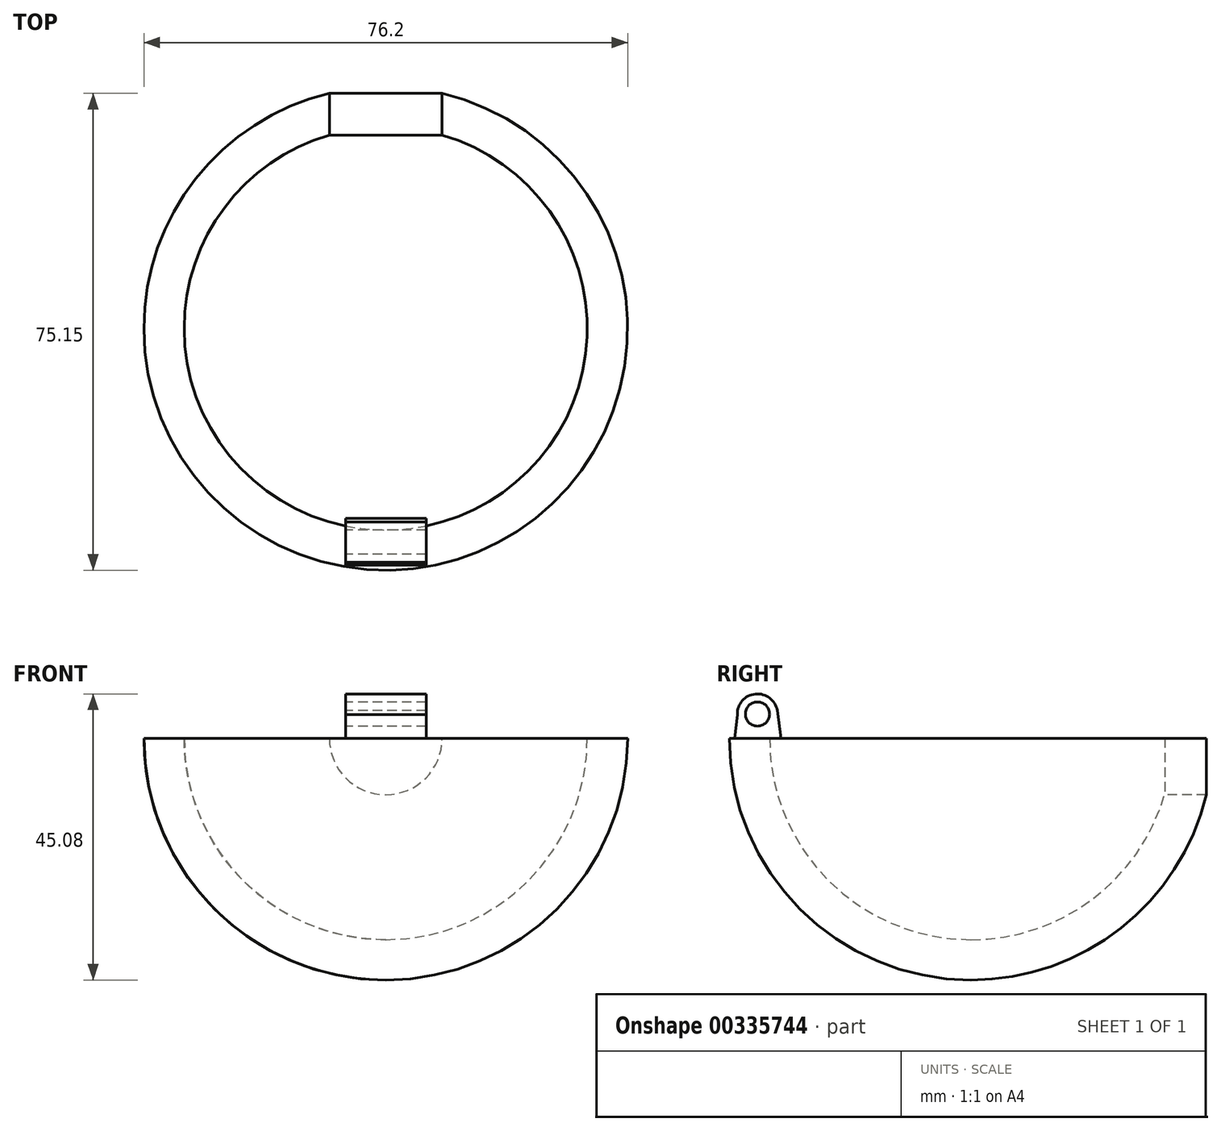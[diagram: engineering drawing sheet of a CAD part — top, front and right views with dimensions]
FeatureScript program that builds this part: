
annotation { "Feature Type Name" : "Feature", "Feature Type Description" : "" }
export const myFeature = defineFeature(function(context is Context, id is Id, definition is map)
    precondition{}
    {
        {
            var Q0;
            Q0=qCreatedBy(makeId("Front.planeOp"),FACE);
            var sketch = newSketch(context, id + "F0", { "sketchPlane" : qUnion([Q0])});
            skArc(sketch, "E0", {"start": v(-38.1, 0) * mm, "mid": v(-26.94, -26.94) * mm, "end": v(0, -38.1) * mm});
            skLineSegment(sketch, "E1", {"start": v(-38.1, 0) * mm, "end": v(-31.75, 0) * mm});
            skLineSegment(sketch, "E2", {"start": v(0, -31.75) * mm, "end": v(0, -38.1) * mm});
            skArc(sketch, "E3.0", {"start": v(-31.75, 0) * mm, "mid": v(-22.45, -22.45) * mm, "end": v(0, -31.75) * mm});
            skSolve(sketch);
        }
        {
            var Q0;
            Q0=makeQuery(id+"F0.imprint","IMPRINT",FACE,{"disambiguationData":[TD([[makeQuery(id+"F0.imprint","IMPRINT",EDGE,{"derivedFrom":sQuery(id+"F0.wireOp",EDGE,"E0")}),1.0]])]});
            var Q1;
            Q1=sQuery(id+"F0.wireOp",EDGE,"E2");
            revolve(context, id + "F1", {"entities" : qUnion([Q0]), "axis" : qUnion([Q1]), "revolveType" : RevolveType.FULL});
        }
        {
            var Q0;
            Q0=qCreatedBy(makeId("Front.planeOp"),FACE);
            var sketch = newSketch(context, id + "F2", { "sketchPlane" : qUnion([Q0])});
            skCircle(sketch, "E4", {"center": v(0, 0) * mm, "radius": 8.9 * mm});
            skSolve(sketch);
        }
        {
            var Q0;
            Q0=makeQuery(id+"F2.imprint","IMPRINT",FACE,{"disambiguationData":[TD([[makeQuery(id+"F2.imprint","IMPRINT",EDGE,{"derivedFrom":sQuery(id+"F2.wireOp",EDGE,"E4")}),1.0]])]});
            extrude(context, id + "F3", {"entities" : qUnion([Q0]), "operationType" : NewBodyOperationType.REMOVE, "endBound" : BoundingType.THROUGH_ALL, "oppositeDirection" : true, "depth" : 25.4 * mm});
        }
        {
            var Q0;
            Q0=qCreatedBy(makeId("Right.planeOp"),FACE);
            var sketch = newSketch(context, id + "F4", { "sketchPlane" : qUnion([Q0])});
            skLineSegment(sketch, "E5.0.0", {"start": v(-31.75, 0) * mm, "end": v(-38.1, 0) * mm});
            skPoint(sketch, "E5.0.3.end.orphan", {"position": v(37.05, 0) * mm});
            skPoint(sketch, "E5.0.3.start.orphan", {"position": v(30.48, 0) * mm});
            skPoint(sketch, "E5.0.1.end.orphan", {"position": v(30.48, 0) * mm});
            skPoint(sketch, "E5.0.1.start.orphan", {"position": v(37.05, 0) * mm});
            skCircle(sketch, "E6", {"center": v(-33.65, 3.8) * mm, "radius": 1.9 * mm});
            skArc(sketch, "E7.0", {"start": v(-30.5, 4.1) * mm, "mid": v(-33.83, 6.98) * mm, "end": v(-36.83, 3.74) * mm});
            skLineSegment(sketch, "E8", {"start": v(-36.83, 3.74) * mm, "end": v(-37.27, 0) * mm});
            skLineSegment(sketch, "E9", {"start": v(-37.27, 0) * mm, "end": v(-29.94, 0) * mm});
            skLineSegment(sketch, "E10", {"start": v(-29.94, 0) * mm, "end": v(-30.53, 4.37) * mm});
            skSolve(sketch);
        }
        {
            var Q0;
            Q0=makeQuery(id+"F4.imprint","IMPRINT",FACE,{"disambiguationData":[TD([[makeQuery(id+"F4.imprint","IMPRINT",EDGE,{"derivedFrom":sQuery(id+"F4.wireOp",EDGE,"E6")}),-1.0]])]});
            extrude(context, id + "F5", {"entities" : qUnion([Q0]), "operationType" : NewBodyOperationType.ADD, "endBound" : BoundingType.SYMMETRIC, "depth" : 12.7 * mm});
        }
    });
